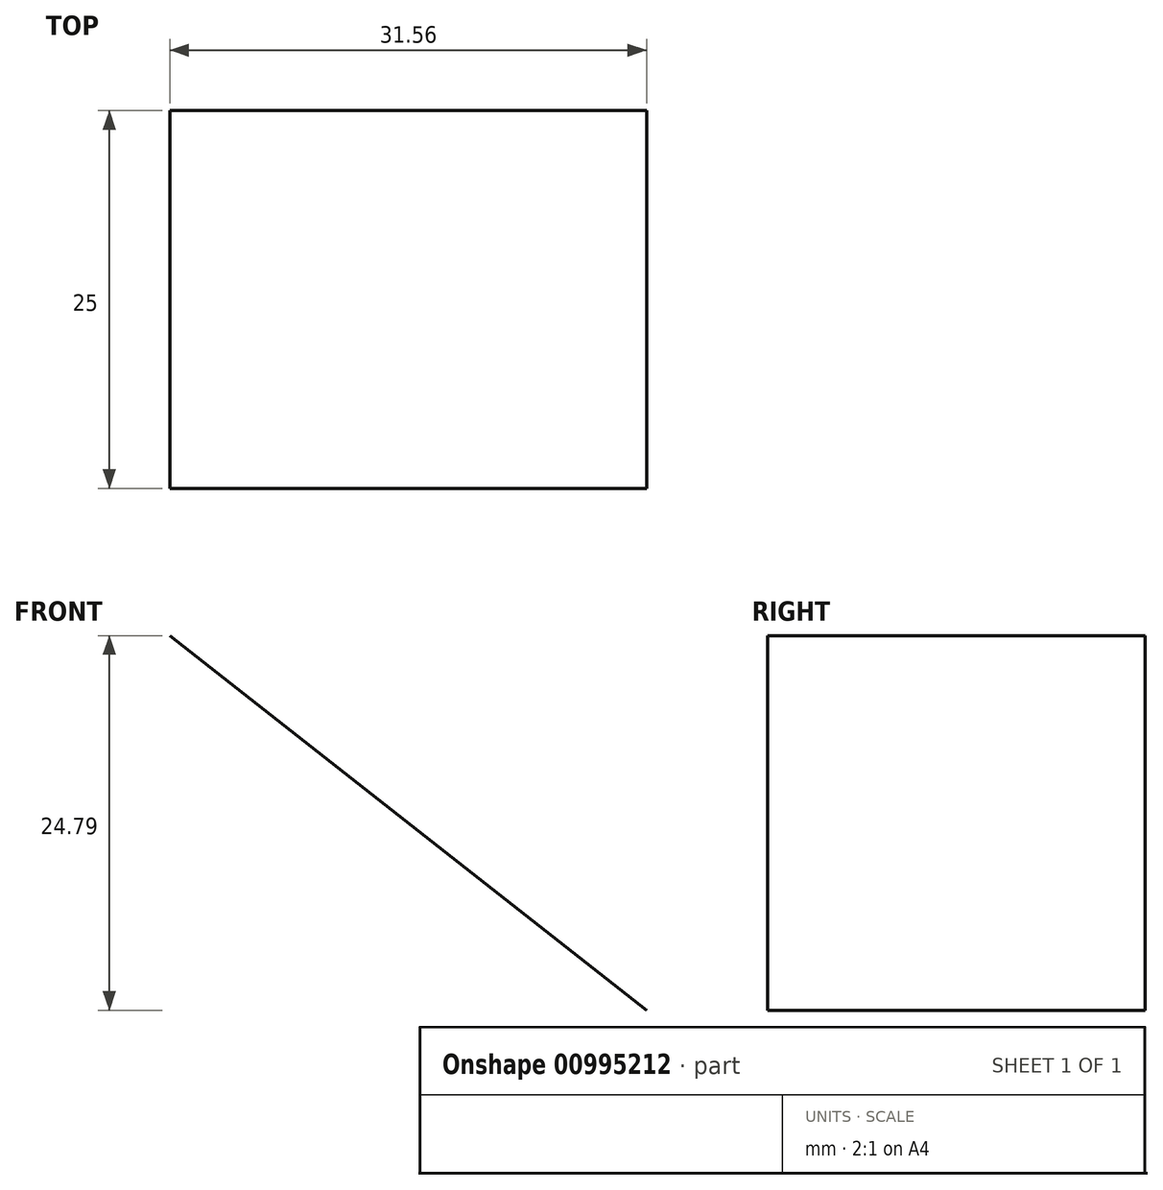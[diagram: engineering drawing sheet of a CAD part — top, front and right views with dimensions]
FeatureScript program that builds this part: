
annotation { "Feature Type Name" : "Feature", "Feature Type Description" : "" }
export const myFeature = defineFeature(function(context is Context, id is Id, definition is map)
    precondition{}
    {
        {
            var Q0;
            Q0=qCreatedBy(makeId("Front.planeOp"),FACE);
            var sketch = newSketch(context, id + "F0", { "sketchPlane" : qUnion([Q0])});
            skLineSegment(sketch, "E0", {"start": v(-97.17, 62.69) * mm, "end": v(-65.6, 37.9) * mm});
            skLineSegment(sketch, "E1.1.0", {"start": v(-5.7, -115.5) * mm, "end": v(-0.02, -75.77) * mm});
            skLineSegment(sketch, "E1.2.0", {"start": v(102.87, 52.8) * mm, "end": v(65.63, 37.87) * mm});
            skPoint(sketch, "E1.center", {"position": v(0, 0) * mm});
            skSolve(sketch);
        }
        {
            var Q0;
            Q0=sQuery(id+"F0.wireOp",EDGE,"E0");
            extrude(context, id + "F1", {"bodyType" : ToolBodyType.SURFACE, "surfaceEntities" : qUnion([Q0]), "depth" : 25 * mm, "offsetDistance" : 25 * mm});
        }
    });
